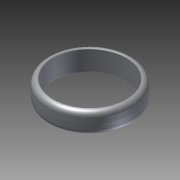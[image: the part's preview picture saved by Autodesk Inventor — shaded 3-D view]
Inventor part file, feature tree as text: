
AUTODESK INVENTOR PART (.ipt)
format: ipt  version: 2011 (Build 150239000, 239)  size: 122,880 bytes
history: native  units: in
note: dims shown in document units (in); Inventor stores cm internally (conversion verified against a paired STEP export)
features: revolve x1, sketch x1
ambient origin geometry x8: Origin, YZ Plane, XZ Plane, XY Plane, X Axis, Y Axis, Z Axis, Center Point
bodies: Solid1 (feature_tree)
feature tree (2):
  revolve  "Revolution1"  [1 undecoded]
  sketch  "Sketch1"  dims[d0=1.5in d1=0.0625in d2=0.375in d3=0.77in d10=3.045in d11=90.0deg]
note: 1 required parameter value undecoded (feature->parameter linkage not recoverable at this tier; creation-order binding heuristic only, values carry confidence <= 0.55)
